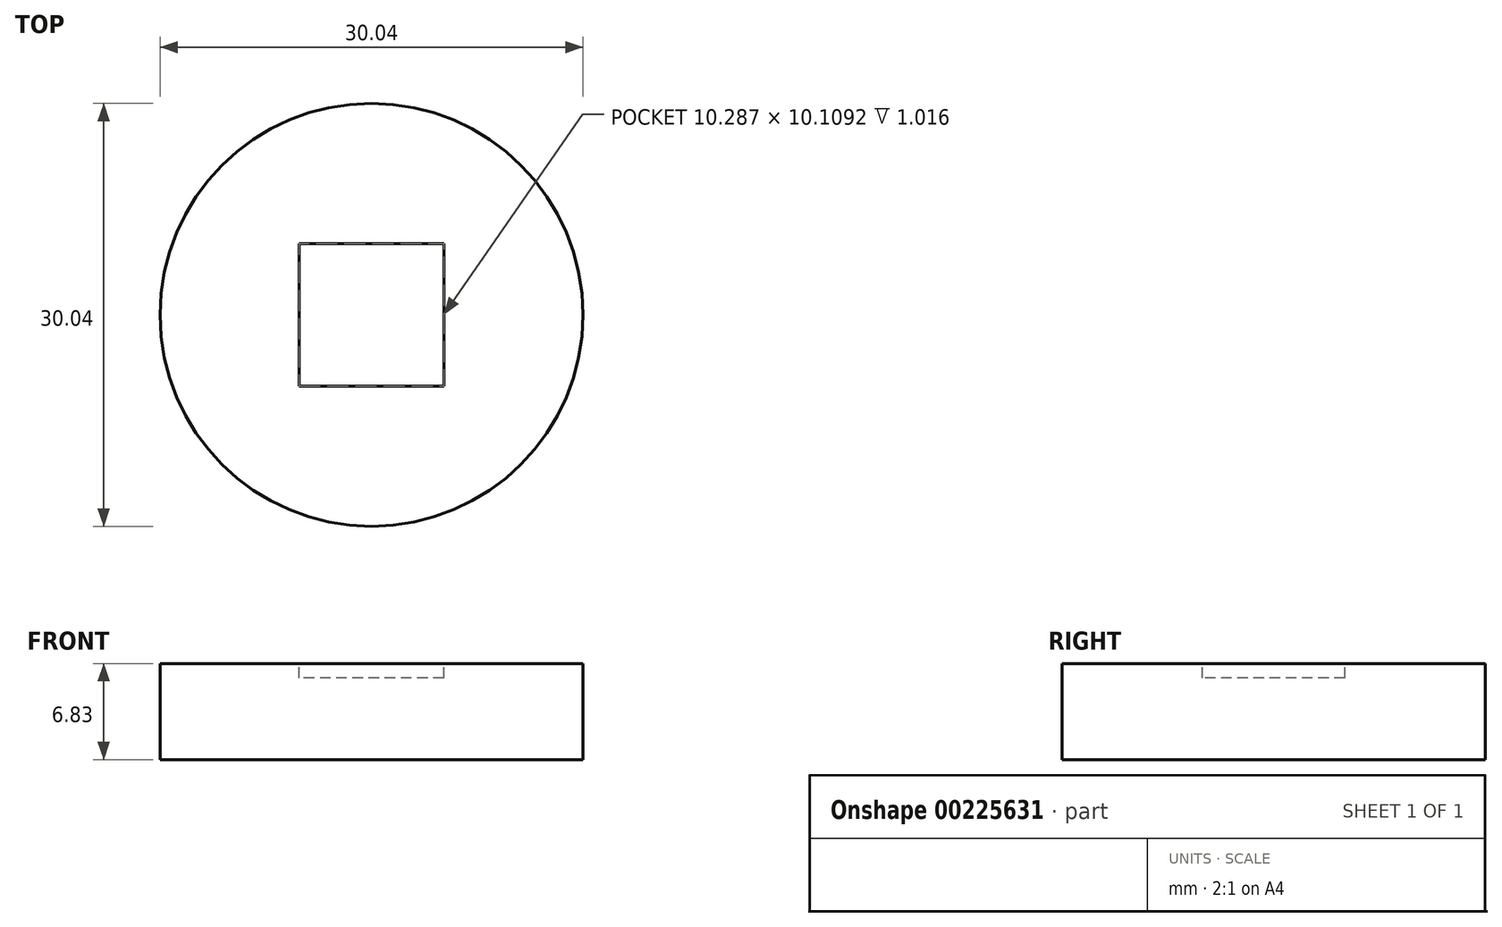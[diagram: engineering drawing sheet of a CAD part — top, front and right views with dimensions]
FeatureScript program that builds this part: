
annotation { "Feature Type Name" : "Feature", "Feature Type Description" : "" }
export const myFeature = defineFeature(function(context is Context, id is Id, definition is map)
    precondition{}
    {
        {
            var Q0;
            Q0=qCreatedBy(makeId("Top.planeOp"),FACE);
            var sketch = newSketch(context, id + "F0", { "sketchPlane" : qUnion([Q0])});
            skCircle(sketch, "E0", {"center": v(0, 0) * mm, "radius": 15.02 * mm});
            skSolve(sketch);
        }
        {
            var Q0;
            Q0 = qSketchRegion(id + "F0", true);
            extrude(context, id + "F1", {"entities" : qUnion([Q0]), "depth" : 6.83 * mm});
        }
        {
            var Q0;
            Q0=makeQuery(id+"F1.opExtrude","CAP_FACE",FACE,{"disambiguationData":[OSD([sQuery(id+"F0.wireOp",EDGE,"E0")])],"isStart":false});
            var sketch = newSketch(context, id + "F2", { "sketchPlane" : qUnion([Q0])});
            skLineSegment(sketch, "E1.bottom", {"start": v(5.14, 5.05) * mm, "end": v(-5.14, 5.05) * mm});
            skLineSegment(sketch, "E1.top", {"start": v(5.14, -5.05) * mm, "end": v(-5.14, -5.05) * mm});
            skLineSegment(sketch, "E1.left", {"start": v(5.14, 5.05) * mm, "end": v(5.14, -5.05) * mm});
            skLineSegment(sketch, "E1.right", {"start": v(-5.14, 5.05) * mm, "end": v(-5.14, -5.05) * mm});
            skPoint(sketch, "E1.middle", {"position": v(0, 0) * mm});
            skSolve(sketch);
        }
        {
            var Q0;
            Q0 = qSketchRegion(id + "F2", true);
            extrude(context, id + "F3", {"entities" : qUnion([Q0]), "operationType" : NewBodyOperationType.REMOVE, "oppositeDirection" : true, "depth" : 2.03 * mm / 2});
        }
    });
